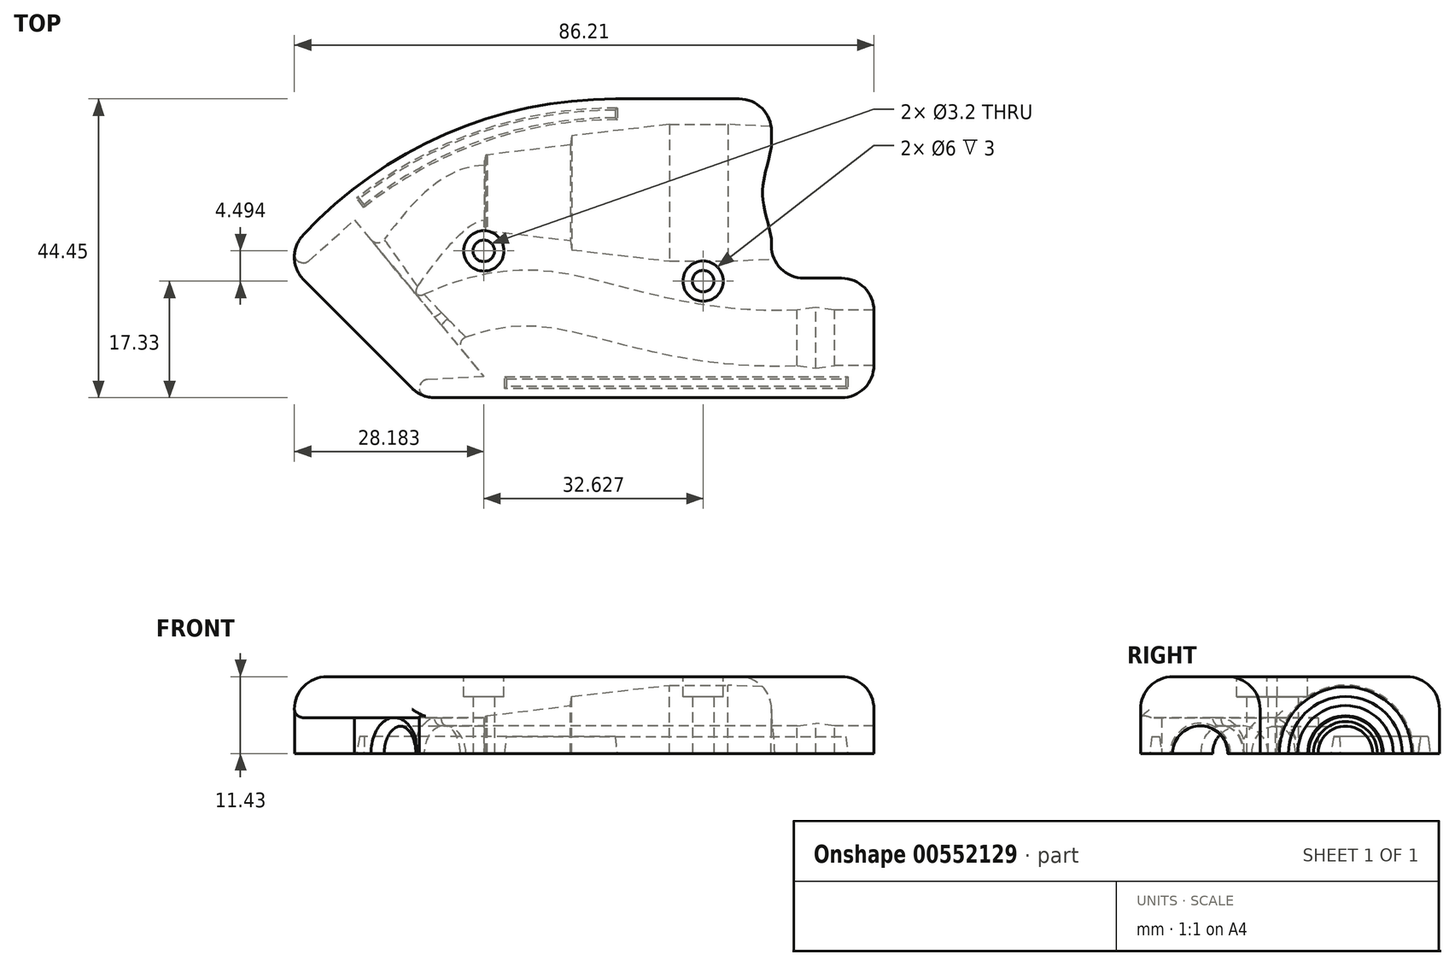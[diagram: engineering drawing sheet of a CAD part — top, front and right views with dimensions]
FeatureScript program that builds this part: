
annotation { "Feature Type Name" : "Feature", "Feature Type Description" : "" }
export const myFeature = defineFeature(function(context is Context, id is Id, definition is map)
    precondition{}
    {
        {
            var Q0;
            Q0=qCreatedBy(makeId("Top.planeOp"),FACE);
            var sketch = newSketch(context, id + "F0", { "sketchPlane" : qUnion([Q0])});
            skLineSegment(sketch, "E0", {"start": v(-26.93, -1.88) * mm, "end": v(47.48, -1.88) * mm});
            skLineSegment(sketch, "E1", {"start": v(47.48, -1.88) * mm, "end": v(47.48, -10.01) * mm});
            skLineSegment(sketch, "E2", {"start": v(47.48, -10.01) * mm, "end": v(35.23, -10.01) * mm});
            skLineSegment(sketch, "E3", {"start": v(35.23, -10.01) * mm, "end": v(33.23, -11.63) * mm});
            skLineSegment(sketch, "E4", {"start": v(33.23, -11.63) * mm, "end": v(18.23, -11.63) * mm});
            skLineSegment(sketch, "E5", {"start": v(18.23, -11.63) * mm, "end": v(9.23, -12.04) * mm});
            skLineSegment(sketch, "E6", {"start": v(9.23, -12.04) * mm, "end": v(0.53, -12.04) * mm});
            skLineSegment(sketch, "E7", {"start": v(0.53, -12.04) * mm, "end": v(-13.97, -10.36) * mm});
            skLineSegment(sketch, "E8", {"start": v(-13.97, -10.36) * mm, "end": v(-14.16, -9) * mm});
            skLineSegment(sketch, "E9", {"start": v(-14.16, -9) * mm, "end": v(-26.57, -7.5) * mm});
            skLineSegment(sketch, "E10", {"start": v(-26.57, -7.5) * mm, "end": v(-26.73, -7.46) * mm});
            skLineSegment(sketch, "E11", {"start": v(-26.73, -7.46) * mm, "end": v(-26.83, -7.36) * mm});
            skLineSegment(sketch, "E12", {"start": v(-26.83, -7.36) * mm, "end": v(-26.95, -6.64) * mm});
            skLineSegment(sketch, "E13", {"start": v(-26.95, -6.64) * mm, "end": v(-26.93, -1.88) * mm});
            skLineSegment(sketch, "E14.bottom", {"start": v(32.13, -23.47) * mm, "end": v(33.23, -23.47) * mm});
            skLineSegment(sketch, "E14.top", {"start": v(32.13, -27.97) * mm, "end": v(33.23, -27.97) * mm});
            skLineSegment(sketch, "E14.left", {"start": v(32.13, -23.47) * mm, "end": v(32.13, -27.97) * mm});
            skLineSegment(sketch, "E14.right", {"start": v(33.23, -23.47) * mm, "end": v(33.23, -27.97) * mm});
            skLineSegment(sketch, "E15.bottom", {"start": v(33.23, -23.47) * mm, "end": v(41.88, -23.47) * mm});
            skLineSegment(sketch, "E15.top", {"start": v(33.23, -26.17) * mm, "end": v(41.88, -26.17) * mm});
            skLineSegment(sketch, "E15.left", {"start": v(33.23, -23.47) * mm, "end": v(33.23, -26.17) * mm});
            skLineSegment(sketch, "E15.right", {"start": v(41.88, -23.47) * mm, "end": v(41.88, -26.17) * mm});
            skLineSegment(sketch, "E16", {"start": v(32.13, -23.47) * mm, "end": v(19.53, -23.47) * mm});
            skLineSegment(sketch, "E17", {"start": v(19.53, -23.47) * mm, "end": v(19.53, -27.6) * mm});
            skLineSegment(sketch, "E18", {"start": v(19.53, -27.6) * mm, "end": v(22.33, -27.97) * mm});
            skLineSegment(sketch, "E19", {"start": v(22.33, -27.97) * mm, "end": v(25.13, -27.6) * mm});
            skLineSegment(sketch, "E20", {"start": v(32.13, -27.6) * mm, "end": v(25.13, -27.6) * mm});
            skLineSegment(sketch, "E21.MirrorCS", {"start": v(32.13, -18.97) * mm, "end": v(33.23, -18.97) * mm});
            skLineSegment(sketch, "E22.MirrorCS", {"start": v(33.23, -23.47) * mm, "end": v(33.23, -18.97) * mm});
            skLineSegment(sketch, "E23.MirrorCS", {"start": v(33.23, -20.77) * mm, "end": v(41.88, -20.77) * mm});
            skLineSegment(sketch, "E24.MirrorCS", {"start": v(33.23, -23.47) * mm, "end": v(33.23, -20.77) * mm});
            skLineSegment(sketch, "E25.MirrorCS", {"start": v(22.33, -18.97) * mm, "end": v(25.13, -19.35) * mm});
            skLineSegment(sketch, "E26.MirrorCS", {"start": v(32.13, -23.47) * mm, "end": v(32.13, -18.97) * mm});
            skLineSegment(sketch, "E27.MirrorCS", {"start": v(41.88, -23.47) * mm, "end": v(41.88, -20.77) * mm});
            skLineSegment(sketch, "E28.MirrorCS", {"start": v(19.53, -23.47) * mm, "end": v(19.53, -19.35) * mm});
            skLineSegment(sketch, "E29.MirrorCS", {"start": v(19.53, -19.35) * mm, "end": v(22.33, -18.97) * mm});
            skLineSegment(sketch, "E30.MirrorCS", {"start": v(32.13, -19.35) * mm, "end": v(25.13, -19.35) * mm});
            skLineSegment(sketch, "E31.MirrorCS", {"start": v(-26.73, 3.69) * mm, "end": v(-26.83, 3.6) * mm});
            skLineSegment(sketch, "E32.MirrorCS", {"start": v(-26.57, 3.74) * mm, "end": v(-26.73, 3.69) * mm});
            skLineSegment(sketch, "E33.MirrorCS", {"start": v(-26.83, 3.6) * mm, "end": v(-26.95, 2.87) * mm});
            skLineSegment(sketch, "E34.MirrorCS", {"start": v(35.23, 6.24) * mm, "end": v(33.23, 7.87) * mm});
            skLineSegment(sketch, "E35.MirrorCS", {"start": v(-13.97, 6.6) * mm, "end": v(-14.16, 5.24) * mm});
            skLineSegment(sketch, "E36.MirrorCS", {"start": v(-26.95, 2.87) * mm, "end": v(-26.93, -1.88) * mm});
            skLineSegment(sketch, "E37.MirrorCS", {"start": v(0.53, 8.28) * mm, "end": v(-13.97, 6.6) * mm});
            skLineSegment(sketch, "E38.MirrorCS", {"start": v(-14.16, 5.24) * mm, "end": v(-26.57, 3.74) * mm});
            skLineSegment(sketch, "E39.MirrorCS", {"start": v(18.23, 7.87) * mm, "end": v(9.23, 8.28) * mm});
            skLineSegment(sketch, "E40.MirrorCS", {"start": v(33.23, 7.87) * mm, "end": v(18.23, 7.87) * mm});
            skLineSegment(sketch, "E41.MirrorCS", {"start": v(47.48, -1.88) * mm, "end": v(47.48, 6.24) * mm});
            skLineSegment(sketch, "E42.MirrorCS", {"start": v(9.23, 8.28) * mm, "end": v(0.53, 8.28) * mm});
            skLineSegment(sketch, "E43.MirrorCS", {"start": v(47.48, 6.24) * mm, "end": v(35.23, 6.24) * mm});
            skSolve(sketch);
        }
        {
            var Q0;
            Q0=qCreatedBy(makeId("Top.planeOp"),FACE);
            var sketch = newSketch(context, id + "F1", { "sketchPlane" : qUnion([Q0])});
            skLineSegment(sketch, "E44", {"start": v(30.97, -32.36) * mm, "end": v(-36.34, -32.36) * mm});
            skLineSegment(sketch, "E45", {"start": v(15.73, 12.09) * mm, "end": v(-7.44, 12.09) * mm});
            skPoint(sketch, "E46.visualSharp", {"position": v(-60.88, 12.09) * mm});
            skArc(sketch, "E46.filletArc", {"start": v(-7.44, 12.09) * mm, "mid": v(-34.92, 5.83) * mm, "end": v(-57, -11.7) * mm});
            skLineSegment(sketch, "E47", {"start": v(15.73, 12.09) * mm, "end": v(15.73, -14.58) * mm});
            skLineSegment(sketch, "E48", {"start": v(15.73, -14.58) * mm, "end": v(30.97, -14.58) * mm});
            skLineSegment(sketch, "E49", {"start": v(30.97, -14.58) * mm, "end": v(30.97, -32.36) * mm});
            skLineSegment(sketch, "E50", {"start": v(-36.34, -32.36) * mm, "end": v(-57, -11.7) * mm});
            skSolve(sketch);
        }
        {
            var Q0;
            Q0=qSketchRegion(id+"F1",true);
            extrude(context, id + "F2", {"entities" : qUnion([Q0]), "depth" : 11.43 * mm, "offsetDistance" : 25.4 * mm});
        }
        {
            var Q0;
            Q0=makeQuery(id+"F0.imprint","IMPRINT",FACE,{"disambiguationData":[TD([[makeQuery(id+"F0.imprint","IMPRINT",EDGE,{"derivedFrom":sQuery(id+"F0.wireOp",EDGE,"E0")}),-1.0]])]});
            var Q1;
            Q1=sQuery(id+"F0.wireOp",EDGE,"E0");
            revolve(context, id + "F3", {"operationType" : NewBodyOperationType.REMOVE, "entities" : qUnion([Q0]), "axis" : qUnion([Q1]), "revolveType" : RevolveType.FULL, "oppositeDirection" : true});
        }
        {
            var Q0;
            Q0=makeQuery(id+"F0.imprint","IMPRINT",FACE,{"disambiguationData":[TD([[makeQuery(id+"F0.imprint","IMPRINT",EDGE,{"derivedFrom":sQuery(id+"F0.wireOp",EDGE,"E15.top")}),1.0]])]});
            var Q1;
            {var subQ2=sQuery(id+"F0.wireOp",EDGE,"E14.top");Q1=makeQuery(id+"F0.imprint","IMPRINT",FACE,{"disambiguationData":[TD([[makeQuery(id+"F0.imprint","IMPRINT",EDGE,{"derivedFrom":subQ2}),1.0]])]});}
            var Q2;
            {var subQ0=sQuery(id+"F0.wireOp",EDGE,"E16");Q2=makeQuery(id+"F0.imprint","IMPRINT",FACE,{"disambiguationData":[TD([[makeQuery(id+"F0.imprint","IMPRINT",EDGE,{"derivedFrom":subQ0}),1.0]])]});}
            var Q3;
            Q3=sQuery(id+"F0.wireOp",EDGE,"E15.bottom");
            revolve(context, id + "F4", {"operationType" : NewBodyOperationType.REMOVE, "entities" : qUnion([Q0, Q1, Q2]), "axis" : qUnion([Q3]), "revolveType" : RevolveType.FULL});
        }
        {
            var Q0;
            Q0=makeQuery(id+"F0.imprint","IMPRINT",FACE,{"disambiguationData":[TD([[makeQuery(id+"F0.imprint","IMPRINT",EDGE,{"derivedFrom":sQuery(id+"F0.wireOp",EDGE,"E0")}),-1.0]])]});
            var sketch = newSketch(context, id + "F5", { "sketchPlane" : qUnion([Q0])});
            skLineSegment(sketch, "E51.0", {"start": v(-26.93, -1.88) * mm, "end": v(47.48, -1.88) * mm});
            skFitSpline(sketch, "E52", {"points": [v(-26.93, -1.88) * mm, v(-43.16, -17.56) * mm, v(-61.68, -40.76) * mm], "startDerivative": vector(-35.8, 0) * mm, "endDerivative": vector(-30.01, -33.42) * mm});
            skSolve(sketch);
        }
        {
            var Q0;
            Q0=sQuery(id+"F5.wireOp",VERTEX,"E51.0.start");
            var Q1;
            Q1=sQuery(id+"F5.wireOp",EDGE,"E51.0");
            cPlane(context, id + "F6", {"entities" : qUnion([Q0, Q1]), "cplaneType" : CPlaneType.LINE_POINT, "offset" : 25.4 * mm, "width" : 152.4 * mm, "height" : 152.4 * mm});
        }
        {
            var Q0;
            Q0=qCreatedBy(id+"F6.planeOp",FACE);
            var sketch = newSketch(context, id + "F7", { "sketchPlane" : qUnion([Q0])});
            skCircle(sketch, "E53", {"center": v(-1.88, 0) * mm, "radius": 4.06 * mm});
            skSolve(sketch);
        }
        {
            var Q0;
            Q0=qSketchRegion(id+"F7",true);
            var Q1;
            Q1=sQuery(id+"F5.wireOp",EDGE,"E52");
            sweep(context, id + "F8", {"operationType" : NewBodyOperationType.REMOVE, "profiles" : qUnion([Q0]), "path" : qUnion([Q1])});
        }
        {
            var Q0;
            Q0=sQuery(id+"F0.wireOp",VERTEX,"E17.start");
            var Q1;
            Q1=sQuery(id+"F0.wireOp",EDGE,"E16");
            cPlane(context, id + "F9", {"entities" : qUnion([Q0, Q1]), "cplaneType" : CPlaneType.LINE_POINT, "offset" : 25.4 * mm, "width" : 152.4 * mm, "height" : 152.4 * mm});
        }
        {
            var Q0;
            Q0=qCreatedBy(id+"F9.planeOp",FACE);
            var sketch = newSketch(context, id + "F10", { "sketchPlane" : qUnion([Q0])});
            skCircle(sketch, "E54", {"center": v(23.47, 0) * mm, "radius": 4.12 * mm});
            skSolve(sketch);
        }
        {
            var Q0;
            Q0=makeQuery(id+"F1.imprint","IMPRINT",FACE,{"disambiguationData":[TD([[makeQuery(id+"F1.imprint","IMPRINT",EDGE,{"derivedFrom":sQuery(id+"F1.wireOp",EDGE,"E44")}),-1.0]])]});
            var sketch = newSketch(context, id + "F11", { "sketchPlane" : qUnion([Q0])});
            skLineSegment(sketch, "E55", {"start": v(-56.34, -14.91) * mm, "end": v(-46.29, -5.92) * mm});
            skLineSegment(sketch, "E56", {"start": v(-46.29, -5.92) * mm, "end": v(-27.06, -29.26) * mm});
            skLineSegment(sketch, "E57", {"start": v(-27.06, -29.26) * mm, "end": v(-42.06, -30.01) * mm});
            skLineSegment(sketch, "E58", {"start": v(-42.06, -30.01) * mm, "end": v(-56.34, -14.91) * mm});
            skSolve(sketch);
        }
        {
            var Q0;
            Q0=qSketchRegion(id+"F11",true);
            extrude(context, id + "F12", {"entities" : qUnion([Q0]), "operationType" : NewBodyOperationType.REMOVE, "depth" : 5.33 * mm, "offsetDistance" : 25.4 * mm});
        }
        {
            var Q0;
            Q0=makeQuery(id+"F1.imprint","IMPRINT",FACE,{"disambiguationData":[TD([[makeQuery(id+"F1.imprint","IMPRINT",EDGE,{"derivedFrom":sQuery(id+"F1.wireOp",EDGE,"E44")}),-1.0]])]});
            var sketch = newSketch(context, id + "F13", { "sketchPlane" : qUnion([Q0])});
            skLineSegment(sketch, "E59.0", {"start": v(32.13, -23.47) * mm, "end": v(19.53, -23.47) * mm});
            skFitSpline(sketch, "E60", {"points": [v(19.53, -23.47) * mm, v(-20.58, -17.52) * mm, v(-45.14, -27.44) * mm, v(-64.46, -44.78) * mm], "startDerivative": vector(-152.85, -5.37) * mm, "endDerivative": vector(-46.75, -40.53) * mm});
            skSolve(sketch);
        }
        {
            var Q0;
            Q0=makeQuery(id+"F10.imprint","IMPRINT",FACE,{"disambiguationData":[TD([[makeQuery(id+"F10.imprint","IMPRINT",EDGE,{"derivedFrom":sQuery(id+"F10.wireOp",EDGE,"E54")}),1.0]])]});
            var Q1;
            Q1=sQuery(id+"F13.wireOp",EDGE,"E60");
            sweep(context, id + "F14", {"operationType" : NewBodyOperationType.REMOVE, "profiles" : qUnion([Q0]), "path" : qUnion([Q1])});
        }
        {
            var Q0;
            Q0=makeQuery(id+"F1.imprint","IMPRINT",FACE,{"disambiguationData":[TD([[makeQuery(id+"F1.imprint","IMPRINT",EDGE,{"derivedFrom":sQuery(id+"F1.wireOp",EDGE,"E44")}),-1.0]])]});
            var sketch = newSketch(context, id + "F15", { "sketchPlane" : qUnion([Q0])});
            skCircle(sketch, "E61", {"center": v(-27.06, -10.54) * mm, "radius": 1.6 * mm});
            skCircle(sketch, "E62", {"center": v(5.57, -15.03) * mm, "radius": 1.6 * mm});
            skSolve(sketch);
        }
        {
            var Q0;
            Q0=qSketchRegion(id+"F15",true);
            extrude(context, id + "F16", {"entities" : qUnion([Q0]), "operationType" : NewBodyOperationType.REMOVE, "depth" : 25.4 * mm, "offsetDistance" : 25.4 * mm});
        }
        {
            var Q0;
            Q0=makeQuery(id+"F1.imprint","IMPRINT",FACE,{"disambiguationData":[TD([[makeQuery(id+"F1.imprint","IMPRINT",EDGE,{"derivedFrom":sQuery(id+"F1.wireOp",EDGE,"E44")}),-1.0]])]});
            var sketch = newSketch(context, id + "F17", { "sketchPlane" : qUnion([Q0])});
            skLineSegment(sketch, "E63.bottom", {"start": v(-23.95, -29.24) * mm, "end": v(27.1, -29.24) * mm});
            skLineSegment(sketch, "E63.top", {"start": v(-23.95, -30.99) * mm, "end": v(27.1, -30.99) * mm});
            skLineSegment(sketch, "E63.left", {"start": v(-23.95, -29.24) * mm, "end": v(-23.95, -30.99) * mm});
            skLineSegment(sketch, "E63.right", {"start": v(27.1, -29.24) * mm, "end": v(27.1, -30.99) * mm});
            skArc(sketch, "E64.0", {"start": v(-7.44, 12.09) * mm, "mid": v(-34.92, 5.83) * mm, "end": v(-57, -11.7) * mm});
            skArc(sketch, "E65.0", {"start": v(-7.22, 10.71) * mm, "mid": v(-27.73, 7.3) * mm, "end": v(-45.98, -2.69) * mm});
            skLineSegment(sketch, "E66", {"start": v(-7.22, 10.71) * mm, "end": v(-7.22, 8.96) * mm});
            skLineSegment(sketch, "E67", {"start": v(-45.98, -2.69) * mm, "end": v(-44.9, -4.06) * mm});
            skArc(sketch, "E68.0", {"start": v(-7.22, 8.96) * mm, "mid": v(-27.16, 5.65) * mm, "end": v(-44.9, -4.06) * mm});
            skSolve(sketch);
        }
        {
            var Q0;
            Q0 = qSketchRegion(id + "F17", true);
            extrude(context, id + "F18", {"entities" : qUnion([Q0]), "operationType" : NewBodyOperationType.REMOVE, "depth" : 2.5 * mm, "offsetDistance" : 25.4 * mm, "hasDraft" : true, "draftAngle" : 7 * degree, "draftPullDirection" : true});
        }
        {
            var Q0;
            Q0=makeQuery(id+"F2.opExtrude","CAP_EDGE",EDGE,{"disambiguationData":[OSD([sQuery(id+"F1.wireOp",EDGE,"E46.filletArc")])],"isStart":false});
            var Q1;
            Q1=makeQuery(id+"F2.opExtrude","SWEPT_EDGE",EDGE,{"disambiguationData":[OSD([sQuery(id+"F1.wireOp",EDGE,"E46.filletArc"),sQuery(id+"F1.wireOp",EDGE,"E50")])]});
            var Q2;
            Q2=makeQuery(id+"F2.opExtrude","CAP_EDGE",EDGE,{"disambiguationData":[OSD([sQuery(id+"F1.wireOp",EDGE,"E50")])],"isStart":false});
            var Q3;
            Q3=makeQuery(id+"F2.opExtrude","SWEPT_EDGE",EDGE,{"disambiguationData":[OSD([sQuery(id+"F1.wireOp",EDGE,"E44"),sQuery(id+"F1.wireOp",EDGE,"E50")])]});
            var Q4;
            Q4=makeQuery(id+"F2.opExtrude","CAP_EDGE",EDGE,{"disambiguationData":[OSD([sQuery(id+"F1.wireOp",EDGE,"E44")])],"isStart":false});
            var Q5;
            Q5=makeQuery(id+"F2.opExtrude","SWEPT_EDGE",EDGE,{"disambiguationData":[OSD([sQuery(id+"F1.wireOp",EDGE,"E44"),sQuery(id+"F1.wireOp",EDGE,"E49")])]});
            var Q6;
            Q6=makeQuery(id+"F2.opExtrude","CAP_EDGE",EDGE,{"disambiguationData":[OSD([sQuery(id+"F1.wireOp",EDGE,"E49")])],"isStart":false});
            var Q7;
            Q7=makeQuery(id+"F2.opExtrude","SWEPT_EDGE",EDGE,{"disambiguationData":[OSD([sQuery(id+"F1.wireOp",EDGE,"E48"),sQuery(id+"F1.wireOp",EDGE,"E49")])]});
            var Q8;
            Q8=makeQuery(id+"F2.opExtrude","SWEPT_EDGE",EDGE,{"disambiguationData":[OSD([sQuery(id+"F1.wireOp",EDGE,"E47"),sQuery(id+"F1.wireOp",EDGE,"E48")])]});
            var Q9;
            Q9=makeQuery(id+"F2.opExtrude","CAP_EDGE",EDGE,{"disambiguationData":[OSD([sQuery(id+"F1.wireOp",EDGE,"E48")])],"isStart":false});
            var Q10;
            Q10=makeQuery(id+"F2.opExtrude","CAP_EDGE",EDGE,{"disambiguationData":[OSD([sQuery(id+"F1.wireOp",EDGE,"E47")])],"isStart":false});
            var Q11;
            Q11=makeQuery(id+"F2.opExtrude","SWEPT_EDGE",EDGE,{"disambiguationData":[OSD([sQuery(id+"F1.wireOp",EDGE,"E45"),sQuery(id+"F1.wireOp",EDGE,"E47")])]});
            var Q12;
            Q12=makeQuery(id+"F2.opExtrude","CAP_EDGE",EDGE,{"disambiguationData":[OSD([sQuery(id+"F1.wireOp",EDGE,"E45")])],"isStart":false});
            fillet(context, id + "F19", {"entities" : qUnion([Q0, Q1, Q2, Q3, Q4, Q5, Q6, Q7, Q8, Q9, Q10, Q11, Q12]), "radius" : 4.83 * mm, "tangentPropagation" : true, "allowEdgeOverflow" : false});
        }
        {
            var Q0;
            Q0=makeQuery(id+"F12.boolean.opBoolean","INTERSECT",EDGE,{"derivedFrom":[makeQuery(id+"F2.opExtrude","SWEPT_FACE",FACE,{"disambiguationData":[OSD([sQuery(id+"F1.wireOp",EDGE,"E50")])]}),makeQuery(id+"F12.opExtrude","CAP_FACE",FACE,{"disambiguationData":[OSD([sQuery(id+"F11.wireOp",EDGE,"E55"),sQuery(id+"F11.wireOp",EDGE,"E56"),sQuery(id+"F11.wireOp",EDGE,"E57"),sQuery(id+"F11.wireOp",EDGE,"E58")])],"isStart":false})]});
            var Q1;
            Q1=makeQuery(id+"F19.opFillet","BLEND_EDGE",EDGE,{"blendedFrom":[makeQuery(id+"F2.opExtrude","SWEPT_EDGE",EDGE,{"disambiguationData":[OSD([sQuery(id+"F1.wireOp",EDGE,"E46.filletArc"),sQuery(id+"F1.wireOp",EDGE,"E50")])]}),makeQuery(id+"F12.boolean.opBoolean","COPY",FACE,{"derivedFrom":makeQuery(id+"F12.opExtrude","CAP_FACE",FACE,{"disambiguationData":[OSD([sQuery(id+"F11.wireOp",EDGE,"E55"),sQuery(id+"F11.wireOp",EDGE,"E56"),sQuery(id+"F11.wireOp",EDGE,"E57"),sQuery(id+"F11.wireOp",EDGE,"E58")])],"isStart":false})})],"blendedInto":[makeQuery(id+"F12.boolean.opBoolean","COPY",FACE,{"derivedFrom":makeQuery(id+"F12.opExtrude","CAP_FACE",FACE,{"disambiguationData":[OSD([sQuery(id+"F11.wireOp",EDGE,"E55"),sQuery(id+"F11.wireOp",EDGE,"E56"),sQuery(id+"F11.wireOp",EDGE,"E57"),sQuery(id+"F11.wireOp",EDGE,"E58")])],"isStart":false})})]});
            var Q2;
            Q2=makeQuery(id+"F19.opFillet","BLEND_EDGE",EDGE,{"blendedFrom":[makeQuery(id+"F2.opExtrude","SWEPT_EDGE",EDGE,{"disambiguationData":[OSD([sQuery(id+"F1.wireOp",EDGE,"E46.filletArc"),sQuery(id+"F1.wireOp",EDGE,"E50")])]}),makeQuery(id+"F12.boolean.opBoolean","COPY",FACE,{"derivedFrom":makeQuery(id+"F12.opExtrude","SWEPT_FACE",FACE,{"disambiguationData":[OSD([sQuery(id+"F11.wireOp",EDGE,"E55")])]})})],"blendedInto":[makeQuery(id+"F12.boolean.opBoolean","COPY",FACE,{"derivedFrom":makeQuery(id+"F12.opExtrude","SWEPT_FACE",FACE,{"disambiguationData":[OSD([sQuery(id+"F11.wireOp",EDGE,"E55")])]})})]});
            var Q3;
            Q3=makeQuery(id+"F12.boolean.opBoolean","INTERSECT",EDGE,{"derivedFrom":[makeQuery(id+"F2.opExtrude","SWEPT_FACE",FACE,{"disambiguationData":[OSD([sQuery(id+"F1.wireOp",EDGE,"E50")])]}),makeQuery(id+"F12.opExtrude","SWEPT_FACE",FACE,{"disambiguationData":[OSD([sQuery(id+"F11.wireOp",EDGE,"E57")])]})]});
            var Q4;
            Q4=makeQuery(id+"F14.boolean.opBoolean","INTERSECT",EDGE,{"derivedFrom":[makeQuery(id+"F12.boolean.opBoolean","COPY",FACE,{"derivedFrom":makeQuery(id+"F12.opExtrude","SWEPT_FACE",FACE,{"disambiguationData":[OSD([sQuery(id+"F11.wireOp",EDGE,"E56")])]})}),makeQuery(id+"F14.opSweep","SWEPT_FACE",FACE,{"disambiguationData":[OSD([sQuery(id+"F10.wireOp",EDGE,"E54"),sQuery(id+"F13.wireOp",EDGE,"E60")])]})]});
            var Q5;
            Q5=makeQuery(id+"F12.boolean.opBoolean","INTERSECT",EDGE,{"derivedFrom":[makeQuery(id+"F8.boolean.opBoolean","COPY",FACE,{"derivedFrom":makeQuery(id+"F8.opSweep","SWEPT_FACE",FACE,{"disambiguationData":[OSD([sQuery(id+"F5.wireOp",EDGE,"E52"),sQuery(id+"F7.wireOp",EDGE,"E53")])]})}),makeQuery(id+"F12.opExtrude","SWEPT_FACE",FACE,{"disambiguationData":[OSD([sQuery(id+"F11.wireOp",EDGE,"E56")])]})]});
            fillet(context, id + "F20", {"entities" : qUnion([Q0, Q1, Q2, Q3, Q4, Q5]), "radius" : 1.27 * mm, "tangentPropagation" : true, "allowEdgeOverflow" : false});
        }
        {
            var Q0;
            Q0=makeQuery(id+"F2.opExtrude","CAP_FACE",FACE,{"disambiguationData":[OSD([sQuery(id+"F1.wireOp",EDGE,"E44"),sQuery(id+"F1.wireOp",EDGE,"E45"),sQuery(id+"F1.wireOp",EDGE,"E46.filletArc"),sQuery(id+"F1.wireOp",EDGE,"E47"),sQuery(id+"F1.wireOp",EDGE,"E48"),sQuery(id+"F1.wireOp",EDGE,"E49"),sQuery(id+"F1.wireOp",EDGE,"E50")])],"isStart":false});
            var sketch = newSketch(context, id + "F21", { "sketchPlane" : qUnion([Q0])});
            skCircle(sketch, "E69.0", {"center": v(-27.06, -10.54) * mm, "radius": 1.6 * mm});
            skCircle(sketch, "E70.0", {"center": v(5.57, -15.03) * mm, "radius": 1.6 * mm});
            skCircle(sketch, "E71", {"center": v(-27.06, -10.54) * mm, "radius": 3 * mm});
            skCircle(sketch, "E72", {"center": v(5.57, -15.03) * mm, "radius": 3 * mm});
            skSolve(sketch);
        }
        {
            var Q0;
            Q0 = qSketchRegion(id + "F21", true);
            extrude(context, id + "F22", {"entities" : qUnion([Q0]), "operationType" : NewBodyOperationType.REMOVE, "oppositeDirection" : true, "depth" : 3 * mm, "offsetDistance" : 25.4 * mm});
        }
    });
